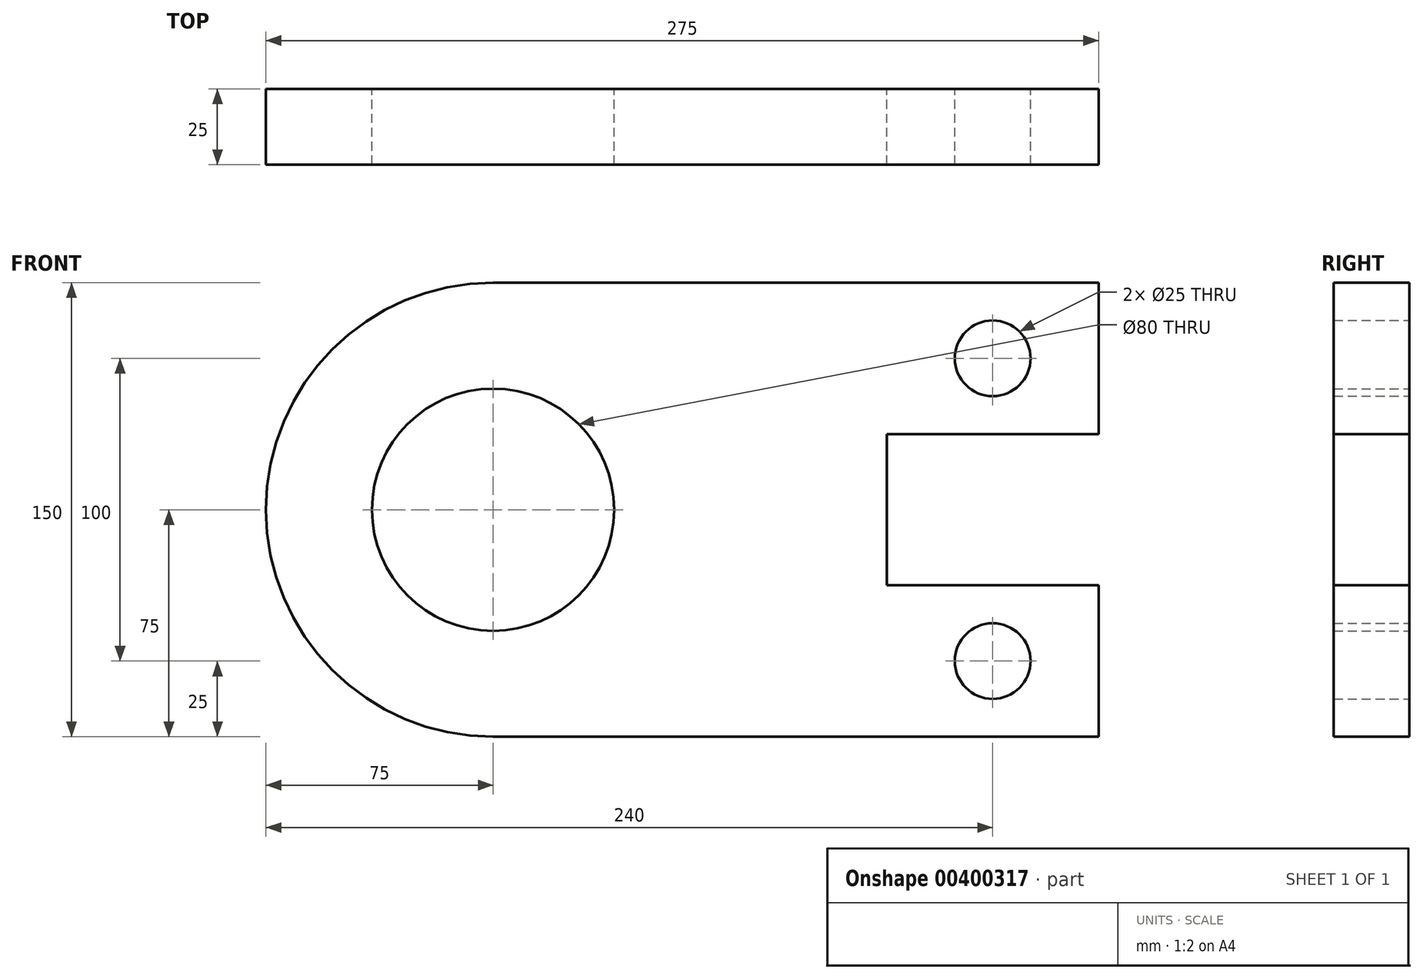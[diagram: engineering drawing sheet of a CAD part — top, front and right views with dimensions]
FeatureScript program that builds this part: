
annotation { "Feature Type Name" : "Feature", "Feature Type Description" : "" }
export const myFeature = defineFeature(function(context is Context, id is Id, definition is map)
    precondition{}
    {
        {
            var Q0;
            Q0=qCreatedBy(makeId("Front.planeOp"),FACE);
            var sketch = newSketch(context, id + "F0", { "sketchPlane" : qUnion([Q0])});
            skCircle(sketch, "E0", {"center": v(0, 0) * mm, "radius": 40 * mm});
            skCircle(sketch, "E1", {"center": v(0, 0) * mm, "radius": 75 * mm});
            skLineSegment(sketch, "E2", {"start": v(0, 0) * mm, "end": v(130, 0) * mm, "construction": true});
            skLineSegment(sketch, "E3", {"start": v(130, 25) * mm, "end": v(200, 25) * mm});
            skLineSegment(sketch, "E4", {"start": v(200, 25) * mm, "end": v(200, 75) * mm});
            skLineSegment(sketch, "E5", {"start": v(200, 75) * mm, "end": v(0, 75) * mm});
            skLineSegment(sketch, "E6", {"start": v(130, 25) * mm, "end": v(130, -25) * mm});
            skLineSegment(sketch, "E7", {"start": v(130, -25) * mm, "end": v(200, -25) * mm});
            skLineSegment(sketch, "E8", {"start": v(200, -25) * mm, "end": v(200, -75) * mm});
            skLineSegment(sketch, "E9", {"start": v(200, -75) * mm, "end": v(0, -75) * mm});
            skLineSegment(sketch, "E10", {"start": v(200, 50) * mm, "end": v(137.28, 50) * mm, "construction": true});
            skCircle(sketch, "E11", {"center": v(165, 50) * mm, "radius": 12.5 * mm});
            skCircle(sketch, "E12.MirrorC", {"center": v(165, -50) * mm, "radius": 12.5 * mm});
            skLineSegment(sketch, "E13.MirrorCS", {"start": v(200, -50) * mm, "end": v(137.28, -50) * mm, "construction": true});
            skSolve(sketch);
        }
        {
            var Q0;
            Q0=makeQuery(id+"F0.imprint","IMPRINT",FACE,{"disambiguationData":[TD([[makeQuery(id+"F0.imprint","IMPRINT",EDGE,{"derivedFrom":sQuery(id+"F0.wireOp",EDGE,"E3")}),1.0]])]});
            var Q1;
            Q1=makeQuery(id+"F0.imprint","IMPRINT",FACE,{"disambiguationData":[TD([[makeQuery(id+"F0.imprint","IMPRINT",EDGE,{"derivedFrom":sQuery(id+"F0.wireOp",EDGE,"E0")}),-1.0]])]});
            extrude(context, id + "F1", {"entities" : qUnion([Q0, Q1]), "depth" : 25 * mm, "offsetDistance" : 25 * mm});
        }
    });
